# Revit family: Screen_Wall-CityScapes-Covrit
name_source: partatom
category: Specialty Equipment
units: mm (PartAtom-declared; Revit-internal decimal feet)

## family parameters
Always vertical = Yes
Cut with Voids When Loaded = No
Enable Cutting in Views = No
Maintain Annotation Orientation = No
Part Type = Normal
Room Calculation Point = No
Round Connector Dimension = Use Diameter
Shared = No
Work Plane-Based = No

## types (3) — shared parameters
CAD Details = https://www.arcat.com
Default Elevation = 0"
Description = Screen Wall
Keynote = 32 35 00
Manufacturer = CityScapes
Model = Covrit Dumpster Walls
Product Page URL = https://www.arcat.com
Specification = https://www.arcat.com
URL = https://cityscapesinc.com
Width = 66"

## per-type parameters (varying)
| type | Height | Post Height |
| 6' Height | 72" | Square_Post-Covrit-CityScapes : Square Post 6' |
| 7' Height | 84" | Square_Post-Covrit-CityScapes : Square Post 7' |
| 8' Height | 96" | Square_Post-Covrit-CityScapes : Square Post 8' |

## geometry (parser evidence)
native form markers: Sweep x7
no freeform markers — native parametric forms only
